# Revit family: NLRS_57_DUA_UN_roof-gland-vpl_LT_velu
name_source: partatom
category: Duct Accessories
units: mm (PartAtom-declared; Revit-internal decimal feet)

## family parameters
Always vertical = No
Cut with Voids When Loaded = No
Part Type = Attaches To
Round Connector Dimension = Use Diameter
Shared = Yes
Work Plane-Based = No

## types (1)
- Plakplaat VPL
    Assembly Code = 57.00
    Description = Velu plakplaat, type VPL
    FireRating = 00
    IfcDescription = Velu plakplaat, type VPL
    IsExternal = Yes
    LoadBearing = No
    LookupTable = VPL_Data
    Manufacturer = Velu Ventilatietechniek BV
    Model = VSK
    NLRS_C_content_datum_uitgifte = 27-05-2022
    NLRS_C_content_provider = Velu Ventliatietechniek BV
    NLRS_C_content_versie = 3.19.00
    NLRS_C_description = Velu plakplaat, type VPL
    NLRS_C_niveau ontwikkeling = LOD400
    URL = https://velu.nl

## geometry (parser evidence)
native form markers: Sweep x4
no freeform markers — native parametric forms only
